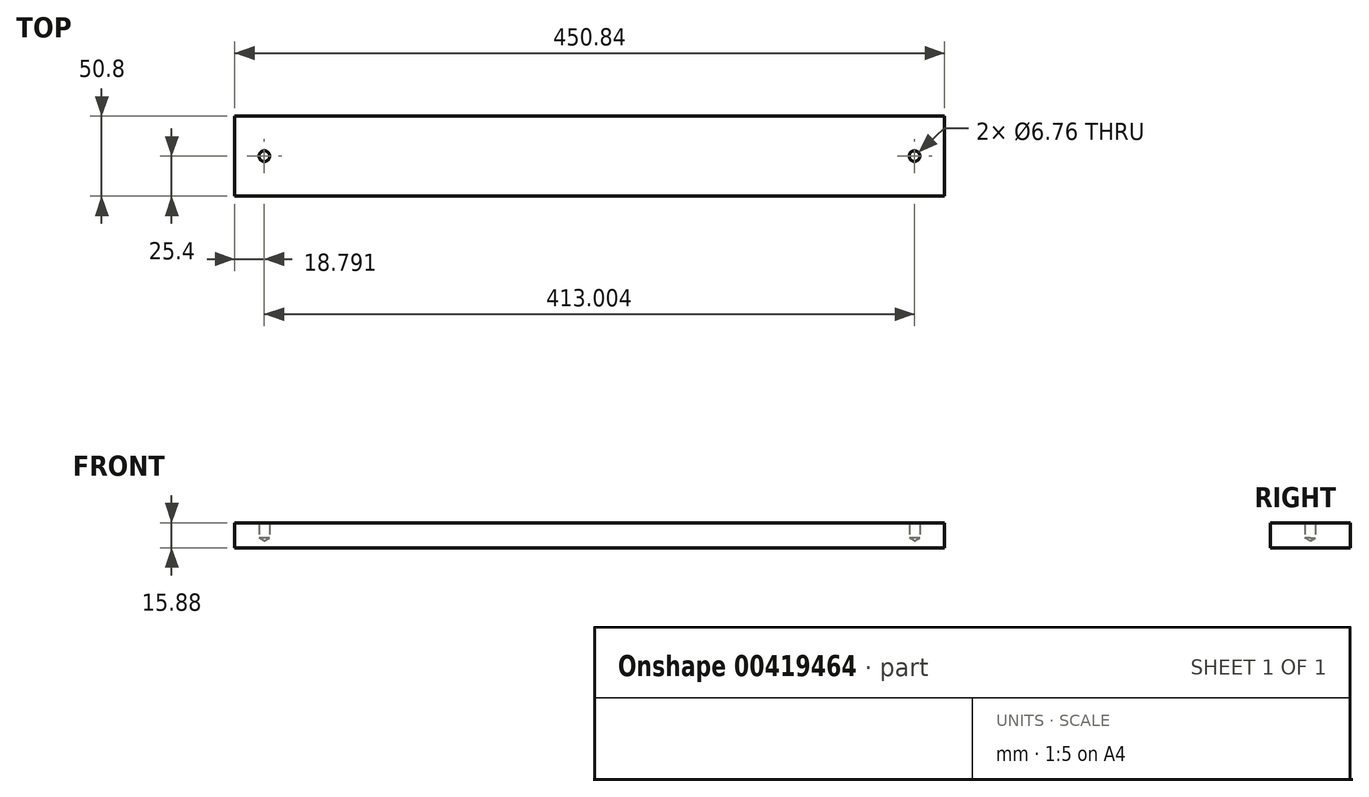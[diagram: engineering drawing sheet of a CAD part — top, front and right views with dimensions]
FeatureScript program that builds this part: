
annotation { "Feature Type Name" : "Feature", "Feature Type Description" : "" }
export const myFeature = defineFeature(function(context is Context, id is Id, definition is map)
    precondition{}
    {
        {
            var Q0;
            Q0=qCreatedBy(makeId("Right.planeOp"),FACE);
            var sketch = newSketch(context, id + "F0", { "sketchPlane" : qUnion([Q0])});
            skLineSegment(sketch, "E0.bottom", {"start": v(-25.4, -7.94) * mm, "end": v(25.4, -7.94) * mm});
            skLineSegment(sketch, "E0.top", {"start": v(-25.4, 7.94) * mm, "end": v(25.4, 7.94) * mm});
            skLineSegment(sketch, "E0.left", {"start": v(-25.4, -7.94) * mm, "end": v(-25.4, 7.94) * mm});
            skLineSegment(sketch, "E0.right", {"start": v(25.4, -7.94) * mm, "end": v(25.4, 7.94) * mm});
            skPoint(sketch, "E0.middle", {"position": v(0, 0) * mm});
            skSolve(sketch);
        }
        {
            var Q0;
            Q0=makeQuery(id+"F0.imprint","IMPRINT",FACE,{"disambiguationData":[TD([[makeQuery(id+"F0.imprint","IMPRINT",EDGE,{"derivedFrom":sQuery(id+"F0.wireOp",EDGE,"E0.bottom")}),1.0]])]});
            extrude(context, id + "F1", {"entities" : qUnion([Q0]), "depth" : 450.85 * mm, "symmetric" : true});
        }
        {
            var Q0;
            Q0=makeQuery(id+"F1.opExtrude","SWEPT_FACE",FACE,{"disambiguationData":[OSD([sQuery(id+"F0.wireOp",EDGE,"E0.top")])]});
            var sketch = newSketch(context, id + "F2", { "sketchPlane" : qUnion([Q0])});
            skPoint(sketch, "E1", {"position": v(206.38, 0) * mm});
            skPoint(sketch, "E1.positionSnap0", {"position": v(225.43, 0) * mm});
            skPoint(sketch, "E2", {"position": v(-206.63, 0) * mm});
            skPoint(sketch, "E2.positionSnap0", {"position": v(-225.43, 0) * mm});
            skSolve(sketch);
        }
        {
            var Q0;
            Q0=sQuery(id+"F2.wireOp",VERTEX,"E1");
            var Q1;
            Q1=sQuery(id+"F2.wireOp",VERTEX,"E2");
            var Q2;
            Q2=makeQuery(id+"F1.opExtrude","SWEPT_BODY",BODY,{"disambiguationData":[OSD([sQuery(id+"F0.wireOp",EDGE,"E0.bottom"),sQuery(id+"F0.wireOp",EDGE,"E0.top"),sQuery(id+"F0.wireOp",EDGE,"E0.left"),sQuery(id+"F0.wireOp",EDGE,"E0.right")])]});
            hole(context, id + "F3", {"style" : HoleStyle.SIMPLE, "endStyle" : HoleEndStyle.BLIND, "standardTappedOrClearance" : lookupTablePath({ "standard" : "ANSI", "fit" : "Normal (ASME)", "size" : "1/4", "type" : "Clearance" }), "standardBlindInLast" : lookupTablePath({ "fit" : "Free", "standard" : "ANSI", "size" : "1/4", "type" : "Clearance" }), "holeDiameter" : 6.76 * mm, "holeDepth" : 9.52 * mm, "locations" : qUnion([Q0, Q1]), "scope" : qUnion([Q2]), "tappedDepth" : 12.7 * mm, "tapClearance" : 3, "startStyle" : HoleStartStyle.SKETCH});
        }
    });
